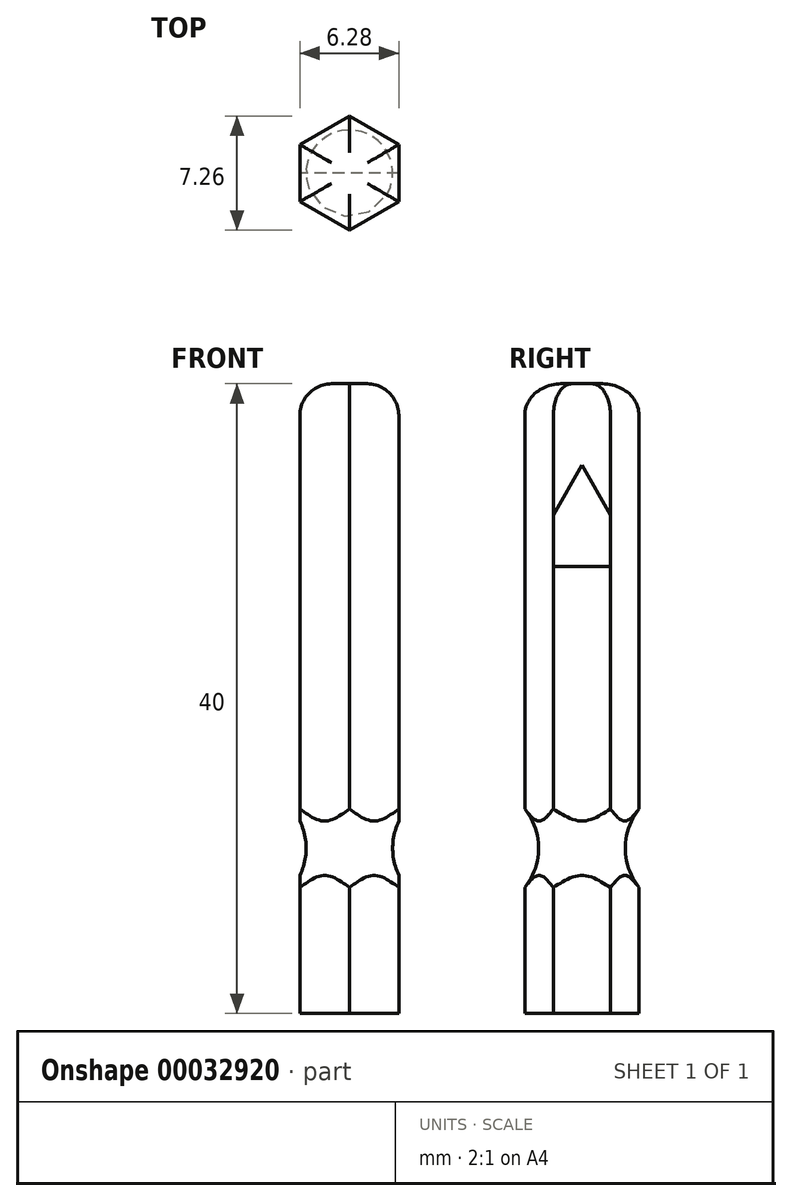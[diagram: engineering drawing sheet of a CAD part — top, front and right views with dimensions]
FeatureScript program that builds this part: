
annotation { "Feature Type Name" : "Feature", "Feature Type Description" : "" }
export const myFeature = defineFeature(function(context is Context, id is Id, definition is map)
    precondition{}
    {
        {
            var Q0;
            Q0=qCreatedBy(makeId("Top.planeOp"),FACE);
            var sketch = newSketch(context, id + "F0", { "sketchPlane" : qUnion([Q0])});
            skCircle(sketch, "E0.cCircle", {"center": v(0, 0) * mm, "radius": 3.14 * mm, "construction": true});
            skLineSegment(sketch, "E0.0", {"start": v(-3.14, 1.81) * mm, "end": v(0, 3.63) * mm});
            skLineSegment(sketch, "E0.1", {"start": v(0, 3.63) * mm, "end": v(3.14, 1.81) * mm});
            skLineSegment(sketch, "E0.2", {"start": v(3.14, 1.81) * mm, "end": v(3.14, -1.81) * mm});
            skLineSegment(sketch, "E0.3", {"start": v(3.14, -1.81) * mm, "end": v(0, -3.63) * mm});
            skLineSegment(sketch, "E0.4", {"start": v(0, -3.63) * mm, "end": v(-3.14, -1.81) * mm});
            skLineSegment(sketch, "E0.5", {"start": v(-3.14, -1.81) * mm, "end": v(-3.14, 1.81) * mm});
            skPoint(sketch, "E0.0.midPoint", {"position": v(-1.57, 2.72) * mm});
            skSolve(sketch);
        }
        {
            var Q0;
            Q0=qSketchRegion(id+"F0",true);
            extrude(context, id + "F1", {"entities" : qUnion([Q0]), "depth" : 40 * mm});
        }
        {
            var Q0;
            Q0=qCreatedBy(makeId("Top.planeOp"),FACE);
            cPlane(context, id + "F2", {"entities" : qUnion([Q0]), "cplaneType" : CPlaneType.OFFSET, "offset" : 10.5 * mm, "width" : 150 * mm, "height" : 150 * mm});
        }
        {
            var Q0;
            Q0=qCreatedBy(id+"F2.planeOp",FACE);
            var sketch = newSketch(context, id + "F3", { "sketchPlane" : qUnion([Q0])});
            skCircle(sketch, "E1", {"center": v(0, 0) * mm, "radius": 6.75 * mm});
            skSolve(sketch);
        }
        {
            var Q0;
            Q0=qCreatedBy(makeId("Front.planeOp"),FACE);
            var sketch = newSketch(context, id + "F4", { "sketchPlane" : qUnion([Q0])});
            skCircle(sketch, "E2", {"center": v(-6.75, 10.5) * mm, "radius": 4 * mm});
            skSolve(sketch);
        }
        {
            var Q0;
            Q0=makeQuery(id+"F4.imprint","IMPRINT",FACE,{"disambiguationData":[TD([[makeQuery(id+"F4.imprint","IMPRINT",EDGE,{"derivedFrom":sQuery(id+"F4.wireOp",EDGE,"E2")}),1.0]])]});
            var Q1;
            Q1=sQuery(id+"F3.wireOp",EDGE,"E1");
            sweep(context, id + "F5", {"operationType" : NewBodyOperationType.REMOVE, "profiles" : qUnion([Q0]), "path" : qUnion([Q1])});
        }
        {
            var Q0;
            Q0=makeQuery(id+"F1.opExtrude","CAP_EDGE",EDGE,{"disambiguationData":[OSD([sQuery(id+"F0.wireOp",EDGE,"E0.3")])],"isStart":false});
            var Q1;
            Q1=makeQuery(id+"F1.opExtrude","CAP_EDGE",EDGE,{"disambiguationData":[OSD([sQuery(id+"F0.wireOp",EDGE,"E0.4")])],"isStart":false});
            var Q2;
            Q2=makeQuery(id+"F1.opExtrude","CAP_EDGE",EDGE,{"disambiguationData":[OSD([sQuery(id+"F0.wireOp",EDGE,"E0.2")])],"isStart":false});
            var Q3;
            Q3=makeQuery(id+"F1.opExtrude","CAP_EDGE",EDGE,{"disambiguationData":[OSD([sQuery(id+"F0.wireOp",EDGE,"E0.0")])],"isStart":false});
            var Q4;
            Q4=makeQuery(id+"F1.opExtrude","CAP_EDGE",EDGE,{"disambiguationData":[OSD([sQuery(id+"F0.wireOp",EDGE,"E0.5")])],"isStart":false});
            var Q5;
            Q5=makeQuery(id+"F1.opExtrude","CAP_EDGE",EDGE,{"disambiguationData":[OSD([sQuery(id+"F0.wireOp",EDGE,"E0.1")])],"isStart":false});
            fillet(context, id + "F6", {"entities" : qUnion([Q0, Q1, Q2, Q3, Q4, Q5]), "radius" : 2 * mm, "tangentPropagation" : true, "allowEdgeOverflow" : false});
        }
        {
            var Q0;
            {var subQ0=sQuery(id+"F0.wireOp",EDGE,"E0.0");var subQ1=sQuery(id+"F0.wireOp",EDGE,"E0.5");var subQ2=sQuery(id+"F0.wireOp",EDGE,"E0.4");Q0=makeQuery(id+"F5.boolean.opBoolean","SPLIT",FACE,{"disambiguationData":[TD([makeQuery(id+"F1.opExtrude","CAP_FACE",FACE,{"disambiguationData":[OSD([subQ0,sQuery(id+"F0.wireOp",EDGE,"E0.1"),sQuery(id+"F0.wireOp",EDGE,"E0.2"),sQuery(id+"F0.wireOp",EDGE,"E0.3"),subQ2,subQ1])],"isStart":false})])],"derivedFrom":makeQuery(id+"F1.opExtrude","SWEPT_FACE",FACE,{"disambiguationData":[OSD([subQ1])]})});}
            var sketch = newSketch(context, id + "F7", { "sketchPlane" : qUnion([Q0])});
            skLineSegment(sketch, "E3", {"start": v(0, 34.84) * mm, "end": v(-1.81, 31.65) * mm});
            skLineSegment(sketch, "E4", {"start": v(-1.81, 31.65) * mm, "end": v(-1.81, 28.4) * mm});
            skLineSegment(sketch, "E5", {"start": v(-1.81, 28.4) * mm, "end": v(1.81, 28.4) * mm});
            skLineSegment(sketch, "E6", {"start": v(1.81, 28.4) * mm, "end": v(1.81, 31.65) * mm});
            skLineSegment(sketch, "E7", {"start": v(1.81, 31.65) * mm, "end": v(0, 34.84) * mm});
            skSolve(sketch);
        }
        {
            var Q0;
            Q0 = qSketchRegion(id + "F7", true);
            extrude(context, id + "F8", {"entities" : qUnion([Q0]), "operationType" : NewBodyOperationType.REMOVE, "endBound" : BoundingType.THROUGH_ALL, "oppositeDirection" : true, "depth" : 25 * mm});
        }
    });
